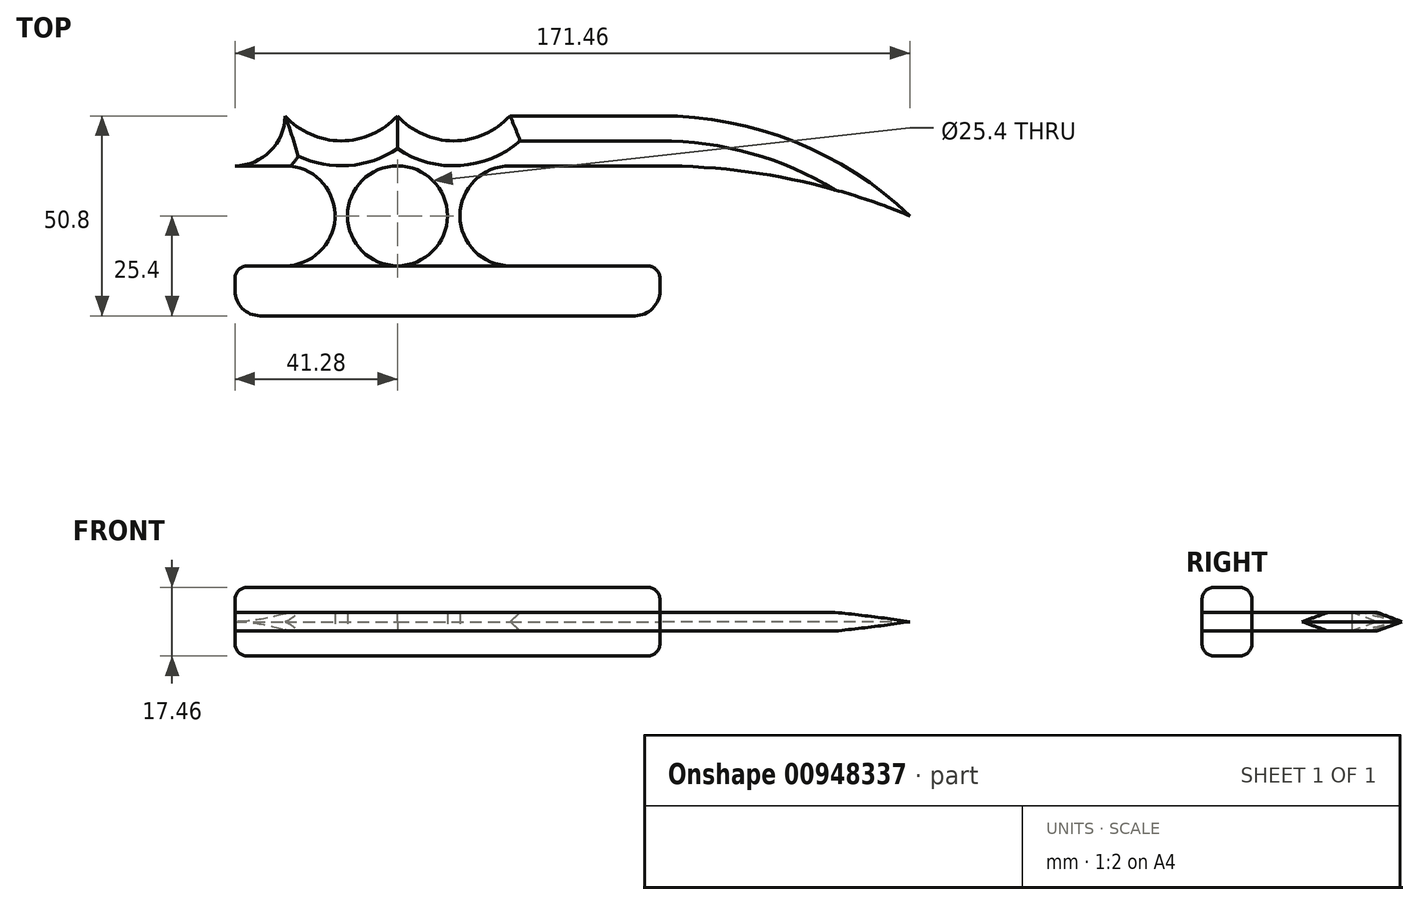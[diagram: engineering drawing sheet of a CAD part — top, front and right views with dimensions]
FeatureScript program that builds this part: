
annotation { "Feature Type Name" : "Feature", "Feature Type Description" : "" }
export const myFeature = defineFeature(function(context is Context, id is Id, definition is map)
    precondition{}
    {
        {
            var Q0;
            Q0=qCreatedBy(makeId("Top.planeOp"),FACE);
            var sketch = newSketch(context, id + "F0", { "sketchPlane" : qUnion([Q0])});
            skArc(sketch, "E0", {"start": v(28.57, 0) * mm, "mid": v(15.88, 12.7) * mm, "end": v(28.57, 25.4) * mm});
            skArc(sketch, "E1", {"start": v(-28.58, 0) * mm, "mid": v(-15.88, 12.7) * mm, "end": v(-28.58, 25.4) * mm});
            skLineSegment(sketch, "E2", {"start": v(28.57, 25.4) * mm, "end": v(66.68, 25.4) * mm});
            skLineSegment(sketch, "E3", {"start": v(-28.58, 0) * mm, "end": v(-38.1, 0) * mm});
            skLineSegment(sketch, "E4", {"start": v(-41.28, -3.18) * mm, "end": v(-41.28, -6.35) * mm});
            skLineSegment(sketch, "E5", {"start": v(-34.93, -12.7) * mm, "end": v(60.33, -12.7) * mm});
            skLineSegment(sketch, "E6", {"start": v(66.68, -6.35) * mm, "end": v(66.68, -3.17) * mm});
            skLineSegment(sketch, "E7", {"start": v(63.5, 0) * mm, "end": v(28.58, 0) * mm});
            skPoint(sketch, "E8.visualSharp", {"position": v(-41.28, 0) * mm});
            skArc(sketch, "E8.filletArc", {"start": v(-38.1, 0) * mm, "mid": v(-40.35, -0.93) * mm, "end": v(-41.28, -3.18) * mm});
            skPoint(sketch, "E9.visualSharp", {"position": v(-41.28, -12.7) * mm});
            skArc(sketch, "E9.filletArc", {"start": v(-41.28, -6.35) * mm, "mid": v(-39.42, -10.84) * mm, "end": v(-34.93, -12.7) * mm});
            skPoint(sketch, "E10.visualSharp", {"position": v(66.68, -12.7) * mm});
            skArc(sketch, "E10.filletArc", {"start": v(60.33, -12.7) * mm, "mid": v(64.82, -10.84) * mm, "end": v(66.68, -6.35) * mm});
            skPoint(sketch, "E11.visualSharp", {"position": v(66.68, 0) * mm});
            skArc(sketch, "E11.filletArc", {"start": v(66.68, -3.17) * mm, "mid": v(65.75, -0.93) * mm, "end": v(63.5, 0) * mm});
            skLineSegment(sketch, "E12", {"start": v(-28.58, 25.4) * mm, "end": v(-41.28, 25.4) * mm});
            skPoint(sketch, "E13", {"position": v(-28.58, 38.1) * mm});
            skPoint(sketch, "E14", {"position": v(0, 38.1) * mm});
            skPoint(sketch, "E15", {"position": v(28.57, 38.1) * mm});
            skLineSegment(sketch, "E16", {"start": v(28.57, 38.1) * mm, "end": v(-28.58, 38.1) * mm, "construction": true});
            skArc(sketch, "E17", {"start": v(-41.28, 25.4) * mm, "mid": v(-32.3, 29.12) * mm, "end": v(-28.58, 38.1) * mm});
            skPoint(sketch, "E18", {"position": v(-14.29, 12.7) * mm});
            skPoint(sketch, "E18.positionSnap0", {"position": v(-15.88, 12.7) * mm});
            skPoint(sketch, "E19", {"position": v(28.57, 12.7) * mm});
            skPoint(sketch, "E20.end.orphan", {"position": v(-14.29, 25.4) * mm});
            skLineSegment(sketch, "E21", {"start": v(28.58, 38.1) * mm, "end": v(28.58, 38.1) * mm});
            skPoint(sketch, "E22.center.orphan", {"position": v(0, 12.7) * mm});
            skCircle(sketch, "E23", {"center": v(0, 12.7) * mm, "radius": 12.7 * mm});
            skPoint(sketch, "E24.end.orphan", {"position": v(-14.29, 31.75) * mm});
            skLineSegment(sketch, "E25", {"start": v(-14.29, 31.75) * mm, "end": v(28.57, 31.75) * mm, "construction": true});
            skArc(sketch, "E26", {"start": v(-28.58, 38.1) * mm, "mid": v(-22.1, 33.4) * mm, "end": v(-14.29, 31.75) * mm});
            skArc(sketch, "E27", {"start": v(-14.29, 31.75) * mm, "mid": v(-6.47, 33.4) * mm, "end": v(0, 38.1) * mm});
            skArc(sketch, "E28", {"start": v(0, 38.1) * mm, "mid": v(14.29, 31.75) * mm, "end": v(28.58, 38.1) * mm});
            skPoint(sketch, "E29", {"position": v(14.29, 31.75) * mm});
            skPoint(sketch, "E29.positionSnap0", {"position": v(14.29, 31.75) * mm});
            skArc(sketch, "E30", {"start": v(130.17, 12.7) * mm, "mid": v(99.05, 22.2) * mm, "end": v(66.68, 25.4) * mm});
            skPoint(sketch, "E31.start.orphan", {"position": v(130.17, 36.2) * mm});
            skLineSegment(sketch, "E32", {"start": v(28.57, 38.1) * mm, "end": v(66.68, 38.1) * mm});
            skArc(sketch, "E33", {"start": v(130.17, 12.7) * mm, "mid": v(100.87, 31.51) * mm, "end": v(66.68, 38.1) * mm});
            skSolve(sketch);
        }
        {
            var Q0;
            Q0 = qSketchRegion(id + "F0", true);
            extrude(context, id + "F1", {"entities" : qUnion([Q0]), "depth" : 4.76 * mm, "offsetDistance" : 25.4 * mm});
        }
        {
            var Q0;
            Q0=qCreatedBy(makeId("Top.planeOp"),FACE);
            var sketch = newSketch(context, id + "F2", { "sketchPlane" : qUnion([Q0])});
            skLineSegment(sketch, "E34.bottom", {"start": v(-38.1, 0) * mm, "end": v(63.5, 0) * mm});
            skLineSegment(sketch, "E34.top", {"start": v(-34.93, -12.7) * mm, "end": v(60.33, -12.7) * mm});
            skLineSegment(sketch, "E34.left", {"start": v(-41.28, -3.18) * mm, "end": v(-41.28, -6.35) * mm});
            skLineSegment(sketch, "E34.right", {"start": v(66.68, -3.18) * mm, "end": v(66.68, -6.35) * mm});
            skPoint(sketch, "E35.visualSharp", {"position": v(-41.28, 0) * mm});
            skArc(sketch, "E35.filletArc", {"start": v(-38.1, 0) * mm, "mid": v(-40.35, -0.93) * mm, "end": v(-41.27, -3.18) * mm});
            skPoint(sketch, "E36.visualSharp", {"position": v(66.68, 0) * mm});
            skArc(sketch, "E36.filletArc", {"start": v(66.68, -3.18) * mm, "mid": v(65.75, -0.93) * mm, "end": v(63.5, 0) * mm});
            skPoint(sketch, "E37.visualSharp", {"position": v(66.68, -12.7) * mm});
            skArc(sketch, "E37.filletArc", {"start": v(60.33, -12.7) * mm, "mid": v(64.82, -10.84) * mm, "end": v(66.68, -6.35) * mm});
            skPoint(sketch, "E38.visualSharp", {"position": v(-41.28, -12.7) * mm});
            skArc(sketch, "E38.filletArc", {"start": v(-41.28, -6.35) * mm, "mid": v(-39.42, -10.84) * mm, "end": v(-34.93, -12.7) * mm});
            skSolve(sketch);
        }
        {
            var Q0;
            Q0 = qSketchRegion(id + "F2", true);
            extrude(context, id + "F3", {"entities" : qUnion([Q0]), "depth" : 11.1 * mm, "offsetDistance" : 25.4 * mm, "hasSecondDirection" : true, "secondDirectionOppositeDirection" : false, "secondDirectionDepth" : 4.76 * mm});
        }
        {
            var Q0;
            Q0=makeQuery(id+"F2.imprint","IMPRINT",FACE,{"disambiguationData":[TD([[makeQuery(id+"F2.imprint","IMPRINT",EDGE,{"derivedFrom":sQuery(id+"F2.wireOp",EDGE,"E34.bottom")}),-1.0]])]});
            extrude(context, id + "F4", {"entities" : qUnion([Q0]), "oppositeDirection" : true, "depth" : 6.35 * mm, "offsetDistance" : 25.4 * mm});
        }
        {
            var Q0;
            Q0=makeQuery(id+"F3.opExtrude","CAP_FACE",FACE,{"disambiguationData":[OSD([sQuery(id+"F2.wireOp",EDGE,"E34.bottom"),sQuery(id+"F2.wireOp",EDGE,"E34.top"),sQuery(id+"F2.wireOp",EDGE,"E34.left"),sQuery(id+"F2.wireOp",EDGE,"E34.right"),sQuery(id+"F2.wireOp",EDGE,"E35.filletArc"),sQuery(id+"F2.wireOp",EDGE,"E36.filletArc"),sQuery(id+"F2.wireOp",EDGE,"E37.filletArc"),sQuery(id+"F2.wireOp",EDGE,"E38.filletArc")])],"isStart":false});
            var Q1;
            Q1=makeQuery(id+"F4.opExtrude","CAP_FACE",FACE,{"disambiguationData":[OSD([sQuery(id+"F2.wireOp",EDGE,"E34.bottom"),sQuery(id+"F2.wireOp",EDGE,"E34.top"),sQuery(id+"F2.wireOp",EDGE,"E34.left"),sQuery(id+"F2.wireOp",EDGE,"E34.right"),sQuery(id+"F2.wireOp",EDGE,"E35.filletArc"),sQuery(id+"F2.wireOp",EDGE,"E36.filletArc"),sQuery(id+"F2.wireOp",EDGE,"E37.filletArc"),sQuery(id+"F2.wireOp",EDGE,"E38.filletArc")])],"isStart":false});
            fillet(context, id + "F5", {"entities" : qUnion([Q0, Q1]), "radius" : 3.17 * mm, "tangentPropagation" : true, "allowEdgeOverflow" : false});
        }
        {
            var Q0;
            Q0=makeQuery(id+"F1.opExtrude","CAP_EDGE",EDGE,{"disambiguationData":[OSD([sQuery(id+"F0.wireOp",EDGE,"E32")])],"isStart":false});
            var Q1;
            Q1=makeQuery(id+"F1.opExtrude","CAP_EDGE",EDGE,{"disambiguationData":[OSD([sQuery(id+"F0.wireOp",EDGE,"E28")])],"isStart":false});
            var Q2;
            Q2=makeQuery(id+"F1.opExtrude","CAP_EDGE",EDGE,{"disambiguationData":[OSD([sQuery(id+"F0.wireOp",EDGE,"E33")])],"isStart":false});
            var Q3;
            Q3=makeQuery(id+"F1.opExtrude","CAP_EDGE",EDGE,{"disambiguationData":[OSD([sQuery(id+"F0.wireOp",EDGE,"E26"),sQuery(id+"F0.wireOp",EDGE,"E27")])],"isStart":false});
            var Q4;
            Q4=makeQuery(id+"F1.opExtrude","CAP_EDGE",EDGE,{"disambiguationData":[OSD([sQuery(id+"F0.wireOp",EDGE,"E17")])],"isStart":false});
            chamfer(context, id + "F6", {"entities" : qUnion([Q0, Q1, Q2, Q3, Q4]), "chamferType" : ChamferType.TWO_OFFSETS, "width1" : 2.38 * mm, "oppositeDirection" : false, "width2" : 6.35 * mm, "tangentPropagation" : true});
        }
        {
            var Q0;
            Q0=makeQuery(id+"F1.opExtrude","CAP_EDGE",EDGE,{"disambiguationData":[OSD([sQuery(id+"F0.wireOp",EDGE,"E17")])],"isStart":true});
            var Q1;
            Q1=makeQuery(id+"F1.opExtrude","CAP_EDGE",EDGE,{"disambiguationData":[OSD([sQuery(id+"F0.wireOp",EDGE,"E26"),sQuery(id+"F0.wireOp",EDGE,"E27")])],"isStart":true});
            var Q2;
            Q2=makeQuery(id+"F1.opExtrude","CAP_EDGE",EDGE,{"disambiguationData":[OSD([sQuery(id+"F0.wireOp",EDGE,"E28")])],"isStart":true});
            var Q3;
            Q3=makeQuery(id+"F1.opExtrude","CAP_EDGE",EDGE,{"disambiguationData":[OSD([sQuery(id+"F0.wireOp",EDGE,"E32")])],"isStart":true});
            var Q4;
            Q4=makeQuery(id+"F1.opExtrude","CAP_EDGE",EDGE,{"disambiguationData":[OSD([sQuery(id+"F0.wireOp",EDGE,"E33")])],"isStart":true});
            chamfer(context, id + "F7", {"entities" : qUnion([Q0, Q1, Q2, Q3, Q4]), "chamferType" : ChamferType.TWO_OFFSETS, "width1" : 2.38 * mm, "oppositeDirection" : true, "width2" : 6.35 * mm, "tangentPropagation" : true});
        }
    });
